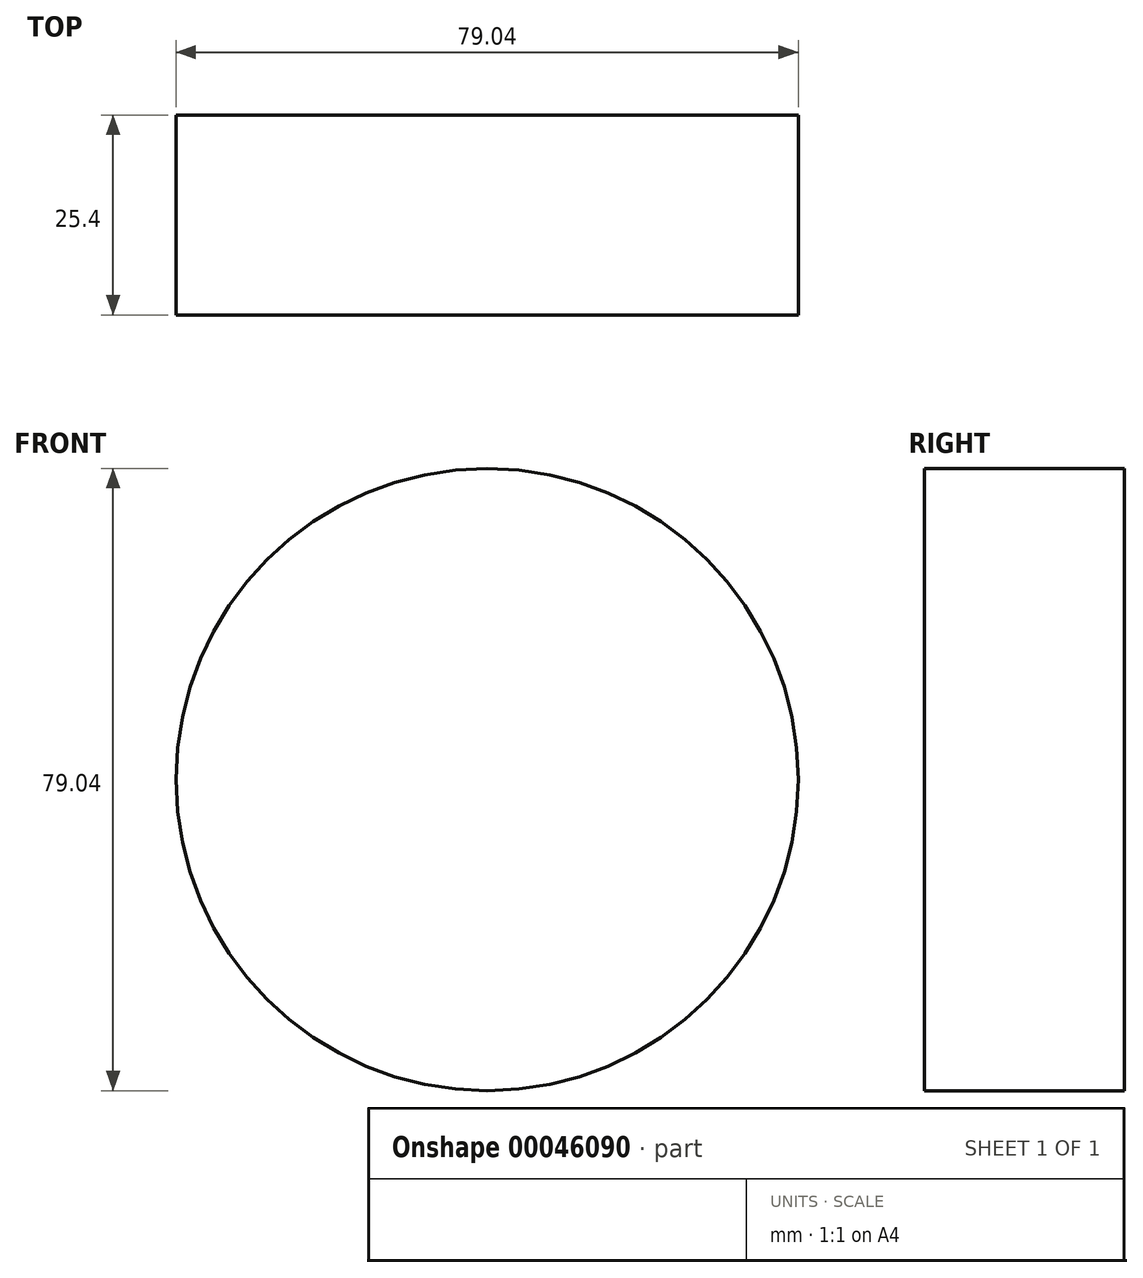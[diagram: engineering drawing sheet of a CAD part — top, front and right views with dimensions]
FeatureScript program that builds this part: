
annotation { "Feature Type Name" : "Feature", "Feature Type Description" : "" }
export const myFeature = defineFeature(function(context is Context, id is Id, definition is map)
    precondition{}
    {
        {
            var Q0;
            Q0=qCreatedBy(makeId("Front.planeOp"),FACE);
            var sketch = newSketch(context, id + "F0", { "sketchPlane" : qUnion([Q0])});
            skCircle(sketch, "E0", {"center": v(0, 0) * mm, "radius": 39.52 * mm});
            skSolve(sketch);
        }
        {
            var Q0;
            Q0 = qSketchRegion(id + "F0", true);
            extrude(context, id + "F1", {"entities" : qUnion([Q0]), "depth" : 25.4 * mm});
        }
    });
